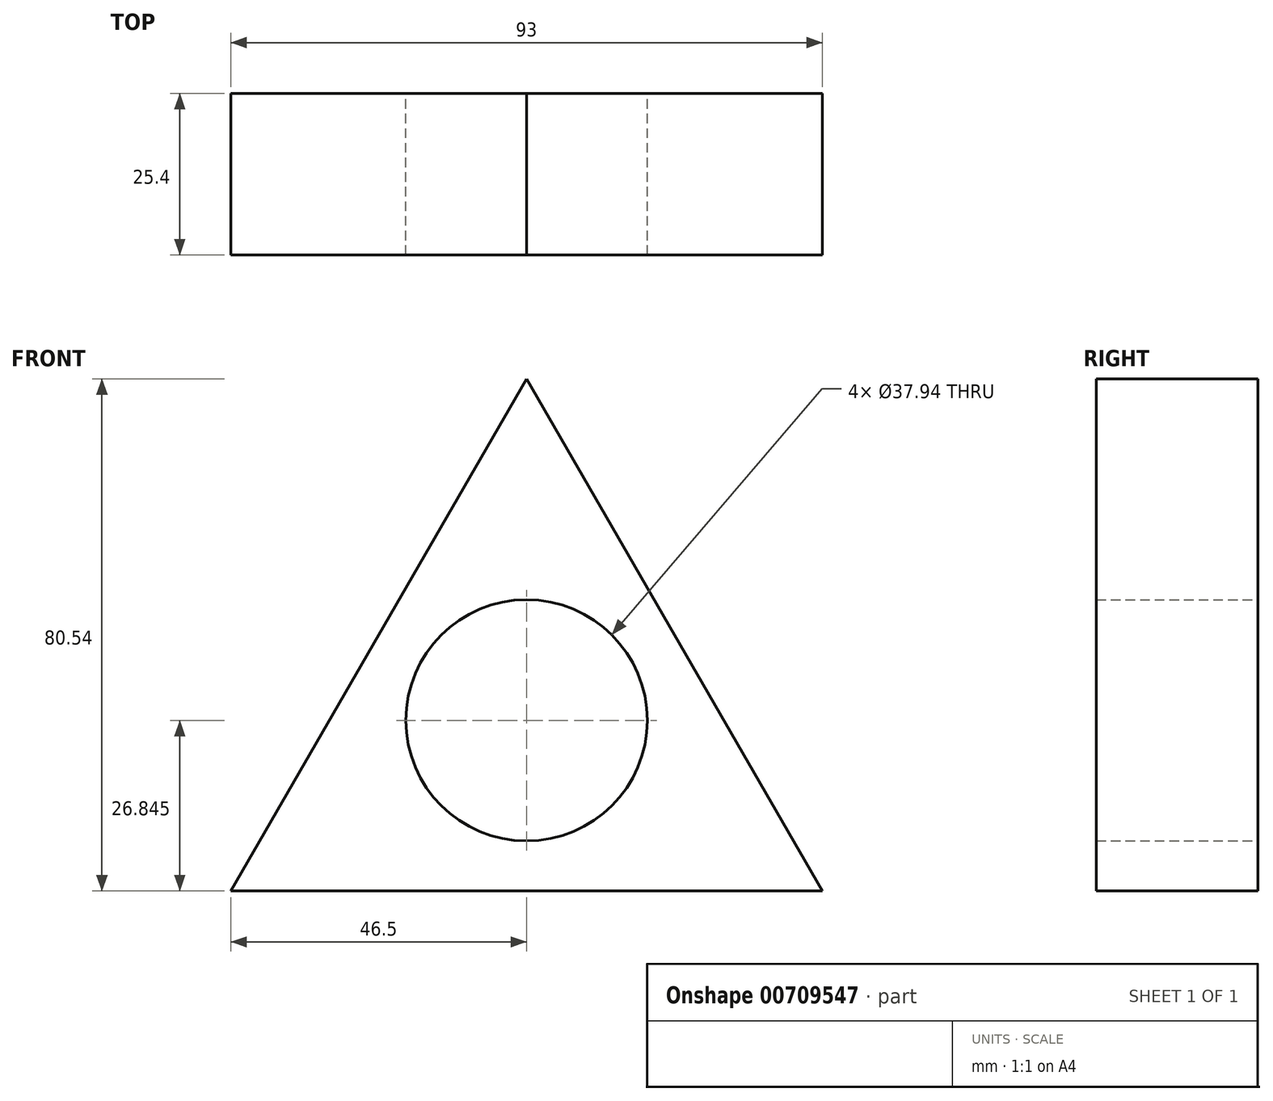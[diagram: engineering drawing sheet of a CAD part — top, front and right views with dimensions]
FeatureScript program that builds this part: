
annotation { "Feature Type Name" : "Feature", "Feature Type Description" : "" }
export const myFeature = defineFeature(function(context is Context, id is Id, definition is map)
    precondition{}
    {
        {
            var Q0;
            Q0=qCreatedBy(makeId("Front.planeOp"),FACE);
            var sketch = newSketch(context, id + "F0", { "sketchPlane" : qUnion([Q0])});
            skCircle(sketch, "E0.cCircle", {"center": v(0, 21.34) * mm, "radius": 26.85 * mm, "construction": true});
            skLineSegment(sketch, "E0.0", {"start": v(46.5, -5.5) * mm, "end": v(-46.5, -5.5) * mm});
            skLineSegment(sketch, "E0.1", {"start": v(-46.5, -5.5) * mm, "end": v(0, 75.04) * mm});
            skLineSegment(sketch, "E0.2", {"start": v(0, 75.04) * mm, "end": v(46.5, -5.5) * mm});
            skPoint(sketch, "E0.0.midPoint", {"position": v(0, -5.5) * mm});
            skCircle(sketch, "E1", {"center": v(0, 21.34) * mm, "radius": 18.97 * mm});
            skSolve(sketch);
        }
        {
            var Q0;
            Q0=makeQuery(id+"F0.imprint","IMPRINT",FACE,{"disambiguationData":[TD([[makeQuery(id+"F0.imprint","IMPRINT",EDGE,{"derivedFrom":sQuery(id+"F0.wireOp",EDGE,"E0.0")}),-1.0]])]});
            extrude(context, id + "F1", {"entities" : qUnion([Q0]), "depth" : 25.4 * mm, "offsetDistance" : 25.4 * mm});
        }
    });
